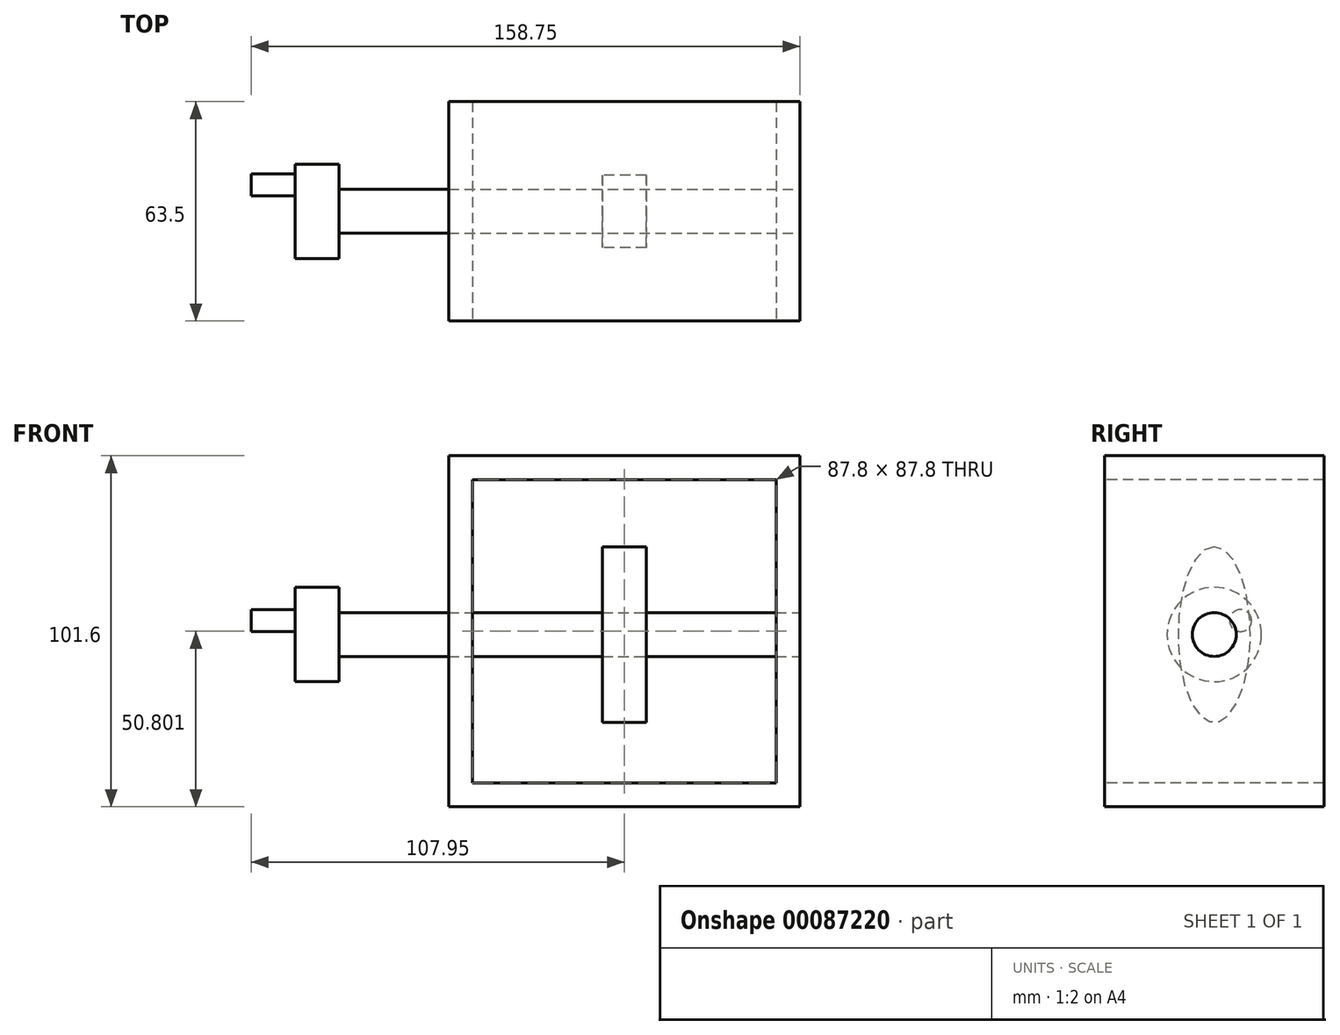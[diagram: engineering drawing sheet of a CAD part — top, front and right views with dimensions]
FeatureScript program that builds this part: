
annotation { "Feature Type Name" : "Feature", "Feature Type Description" : "" }
export const myFeature = defineFeature(function(context is Context, id is Id, definition is map)
    precondition{}
    {
        {
            var Q0;
            Q0=qCreatedBy(makeId("Front.planeOp"),FACE);
            var sketch = newSketch(context, id + "F0", { "sketchPlane" : qUnion([Q0])});
            skLineSegment(sketch, "E0.bottom", {"start": v(-50.8, 51.72) * mm, "end": v(50.8, 51.72) * mm});
            skLineSegment(sketch, "E0.top", {"start": v(-50.8, -49.88) * mm, "end": v(50.8, -49.88) * mm});
            skLineSegment(sketch, "E0.left", {"start": v(-50.8, 51.72) * mm, "end": v(-50.8, -49.88) * mm});
            skLineSegment(sketch, "E0.right", {"start": v(50.8, 51.72) * mm, "end": v(50.8, -49.88) * mm});
            skSolve(sketch);
        }
        {
            var Q0;
            Q0=makeQuery(id+"F0.imprint","IMPRINT",FACE,{"disambiguationData":[TD([[makeQuery(id+"F0.imprint","IMPRINT",EDGE,{"derivedFrom":sQuery(id+"F0.wireOp",EDGE,"E0.bottom")}),-1.0]])]});
            extrude(context, id + "F1", {"entities" : qUnion([Q0]), "endBound" : BoundingType.SYMMETRIC, "depth" : 63.5 * mm});
        }
        {
            var Q0;
            Q0=makeQuery(id+"F1.opExtrude","CAP_FACE",FACE,{"disambiguationData":[OSD([sQuery(id+"F0.wireOp",EDGE,"E0.bottom"),sQuery(id+"F0.wireOp",EDGE,"E0.top"),sQuery(id+"F0.wireOp",EDGE,"E0.left"),sQuery(id+"F0.wireOp",EDGE,"E0.right")])],"isStart":false});
            var sketch = newSketch(context, id + "F2", { "sketchPlane" : qUnion([Q0])});
            skLineSegment(sketch, "E1.0", {"start": v(-43.9, 44.82) * mm, "end": v(43.9, 44.82) * mm});
            skLineSegment(sketch, "E1.1", {"start": v(-43.9, 44.82) * mm, "end": v(-43.9, -42.98) * mm});
            skLineSegment(sketch, "E1.2", {"start": v(-43.9, -42.98) * mm, "end": v(43.9, -42.98) * mm});
            skLineSegment(sketch, "E1.3", {"start": v(43.9, 44.82) * mm, "end": v(43.9, -42.98) * mm});
            skLineSegment(sketch, "E2.0", {"start": v(44.45, 45.37) * mm, "end": v(-44.45, 45.37) * mm});
            skLineSegment(sketch, "E2.1", {"start": v(44.45, -43.53) * mm, "end": v(44.45, 45.37) * mm});
            skLineSegment(sketch, "E2.2", {"start": v(-44.45, -43.53) * mm, "end": v(44.45, -43.53) * mm});
            skLineSegment(sketch, "E2.3", {"start": v(-44.45, 45.37) * mm, "end": v(-44.45, -43.53) * mm});
            skSolve(sketch);
        }
        {
            var Q0;
            Q0=makeQuery(id+"F2.imprint","IMPRINT",FACE,{"disambiguationData":[TD([[makeQuery(id+"F2.imprint","IMPRINT",EDGE,{"derivedFrom":sQuery(id+"F2.wireOp",EDGE,"E1.0")}),-1.0]])]});
            extrude(context, id + "F3", {"entities" : qUnion([Q0]), "operationType" : NewBodyOperationType.REMOVE, "oppositeDirection" : true, "depth" : 101.6 * mm});
        }
        {
            var Q0;
            Q0=makeQuery(id+"F1.opExtrude","SWEPT_FACE",FACE,{"disambiguationData":[OSD([sQuery(id+"F0.wireOp",EDGE,"E0.left")])]});
            var sketch = newSketch(context, id + "F4", { "sketchPlane" : qUnion([Q0])});
            skCircle(sketch, "E3", {"center": v(0, 0) * mm, "radius": 6.35 * mm});
            skSolve(sketch);
        }
        {
            var Q0;
            Q0 = qSketchRegion(id + "F4", true);
            var Q1;
            Q1=sQuery(id+"F4.wireOp",EDGE,"E3");
            var Q2;
            Q2=makeQuery(id+"F1.opExtrude","SWEPT_FACE",FACE,{"disambiguationData":[OSD([sQuery(id+"F0.wireOp",EDGE,"E0.right")])]});
            extrude(context, id + "F5", {"entities" : qUnion([Q0]), "surfaceEntities" : qUnion([Q1]), "depth" : 44.45 * mm, "hasSecondDirection" : true, "secondDirectionBound" : SecondDirectionBoundingType.UP_TO_SURFACE, "secondDirectionOppositeDirection" : true, "secondDirectionBoundEntityFace" : qUnion([Q2]), "secondDirectionDepth" : 25.4 * mm});
        }
        {
            var Q0;
            Q0=makeQuery(id+"F1.opExtrude","SWEPT_FACE",FACE,{"disambiguationData":[OSD([sQuery(id+"F0.wireOp",EDGE,"E0.bottom")])]});
            var sketch = newSketch(context, id + "F6", { "sketchPlane" : qUnion([Q0])});
            skSolve(sketch);
        }
        {
            var Q0;
            {var subQ0=sQuery(id+"F0.wireOp",EDGE,"E0.bottom");Q0=makeQuery(id+"F6.imprint","IMPRINT",FACE,{"disambiguationData":[TD([[makeQuery(id+"F6.imprint","IMPRINT",EDGE,{"derivedFrom":makeQuery(id+"F1.opExtrude","CAP_EDGE",EDGE,{"disambiguationData":[OSD([subQ0])],"isStart":true})}),-1.0]])]});}
            var sketch = newSketch(context, id + "F7", { "sketchPlane" : qUnion([Q0])});
            skCircle(sketch, "E4", {"center": v(0, 0) * mm, "radius": 4.45 * mm});
            skSolve(sketch);
        }
        {
            var Q0;
            Q0=qCreatedBy(makeId("Right.planeOp"),FACE);
            var sketch = newSketch(context, id + "F8", { "sketchPlane" : qUnion([Q0])});
            skEllipse(sketch, "E5", {"center": v(0, 0) * mm, "majorRadius": 25.4 * mm, "minorRadius": 10.46 * mm, "majorAxis": v(0, 1)});
            skSolve(sketch);
        }
        {
            var Q0;
            Q0=makeQuery(id+"F8.imprint","IMPRINT",FACE,{"disambiguationData":[TD([[makeQuery(id+"F8.imprint","IMPRINT",EDGE,{"derivedFrom":sQuery(id+"F8.wireOp",EDGE,"E5")}),1.0]])]});
            extrude(context, id + "F9", {"entities" : qUnion([Q0]), "endBound" : BoundingType.SYMMETRIC, "depth" : 12.7 * mm});
        }
        {
            var Q0;
            Q0=sQuery(id+"F7.wireOp",EDGE,"E4");
            extrude(context, id + "F10", {"bodyType" : ToolBodyType.SURFACE, "surfaceEntities" : qUnion([Q0]), "oppositeDirection" : true, "depth" : 31.75 * mm, "hasSecondDirection" : true, "secondDirectionOppositeDirection" : false, "secondDirectionDepth" : 25.4 * mm});
        }
        {
            var Q0;
            Q0=makeQuery(id+"F5.opExtrude","CAP_FACE",FACE,{"disambiguationData":[OSD([sQuery(id+"F4.wireOp",EDGE,"E3")])],"isStart":false});
            var sketch = newSketch(context, id + "F11", { "sketchPlane" : qUnion([Q0])});
            skCircle(sketch, "E6", {"center": v(0, 0) * mm, "radius": 13.65 * mm});
            skSolve(sketch);
        }
        {
            var Q0;
            Q0=makeQuery(id+"F11.imprint","IMPRINT",FACE,{"disambiguationData":[TD([[makeQuery(id+"F11.imprint","IMPRINT",EDGE,{"derivedFrom":sQuery(id+"F11.wireOp",EDGE,"E6")}),1.0]])]});
            var Q1;
            Q1=sQuery(id+"F11.wireOp",EDGE,"E6");
            extrude(context, id + "F12", {"entities" : qUnion([Q0]), "operationType" : NewBodyOperationType.ADD, "surfaceEntities" : qUnion([Q1]), "oppositeDirection" : true, "depth" : 12.7 * mm});
        }
        {
            var Q0;
            {var subQ0=sQuery(id+"F4.wireOp",EDGE,"E3");Q0=makeQuery(id+"F12.boolean.opBoolean","MERGE",FACE,{"derivedFrom":[makeQuery(id+"F5.opExtrude","CAP_FACE",FACE,{"disambiguationData":[OSD([subQ0])],"isStart":false}),makeQuery(id+"F12.opExtrude","CAP_FACE",FACE,{"disambiguationData":[OSD([subQ0,sQuery(id+"F11.wireOp",EDGE,"E6")])],"isStart":true})]});}
            var sketch = newSketch(context, id + "F13", { "sketchPlane" : qUnion([Q0])});
            skCircle(sketch, "E7", {"center": v(-7.63, 4.02) * mm, "radius": 3.17 * mm});
            skSolve(sketch);
        }
        {
            var Q0;
            Q0=makeQuery(id+"F13.imprint","IMPRINT",FACE,{"disambiguationData":[TD([[makeQuery(id+"F13.imprint","IMPRINT",EDGE,{"derivedFrom":sQuery(id+"F13.wireOp",EDGE,"E7")}),1.0]])]});
            var Q1;
            Q1=sQuery(id+"F13.wireOp",EDGE,"E7");
            extrude(context, id + "F14", {"entities" : qUnion([Q0]), "operationType" : NewBodyOperationType.ADD, "surfaceEntities" : qUnion([Q1]), "depth" : 12.7 * mm});
        }
    });
